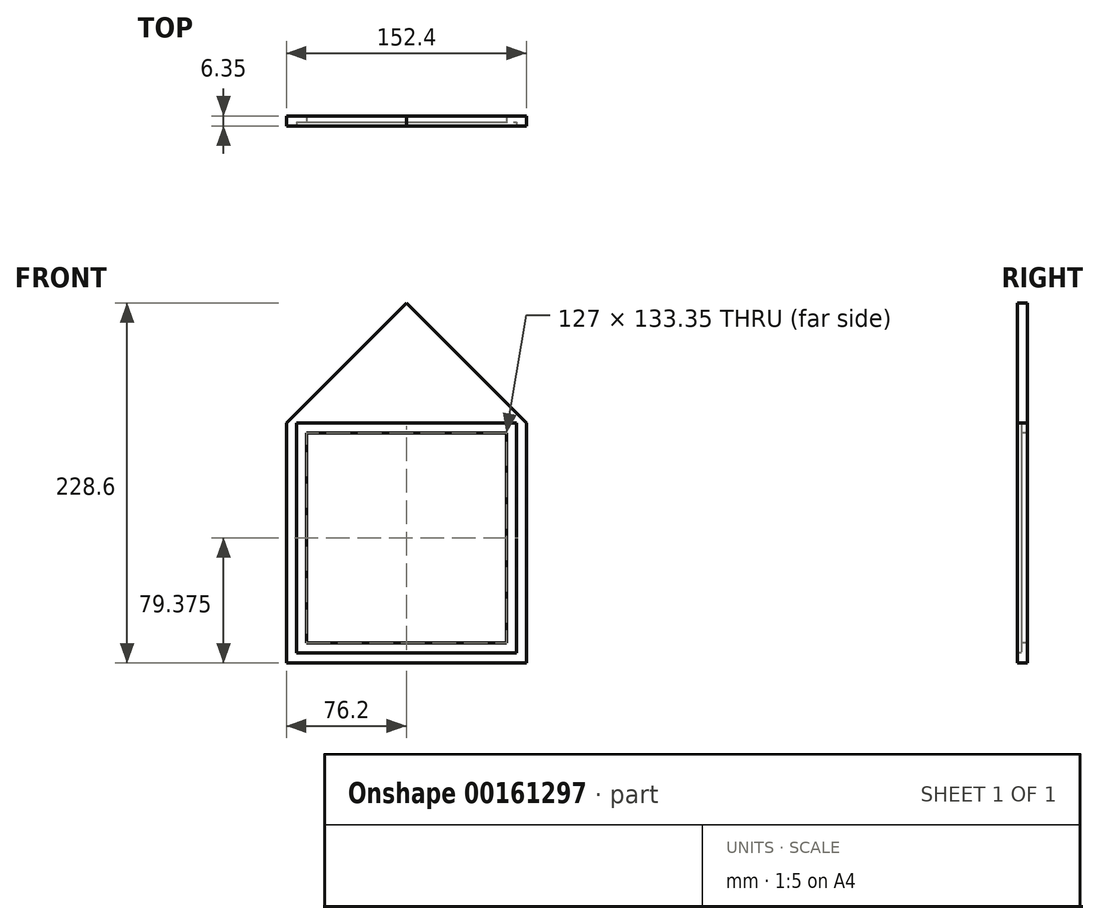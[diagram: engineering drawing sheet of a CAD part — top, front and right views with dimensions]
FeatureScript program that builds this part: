
annotation { "Feature Type Name" : "Feature", "Feature Type Description" : "" }
export const myFeature = defineFeature(function(context is Context, id is Id, definition is map)
    precondition{}
    {
        {
            var Q0;
            Q0=qCreatedBy(makeId("Front.planeOp"),FACE);
            var sketch = newSketch(context, id + "F0", { "sketchPlane" : qUnion([Q0])});
            skLineSegment(sketch, "E0.bottom", {"start": v(0, 0) * mm, "end": v(152.4, 0) * mm});
            skLineSegment(sketch, "E0.top", {"start": v(0, -152.4) * mm, "end": v(152.4, -152.4) * mm});
            skLineSegment(sketch, "E0.left", {"start": v(0, 0) * mm, "end": v(0, -152.4) * mm});
            skLineSegment(sketch, "E0.right", {"start": v(152.4, 0) * mm, "end": v(152.4, -152.4) * mm});
            skLineSegment(sketch, "E1", {"start": v(0, 0) * mm, "end": v(76.2, 76.2) * mm});
            skLineSegment(sketch, "E2", {"start": v(76.2, 76.2) * mm, "end": v(152.4, 0) * mm});
            skSolve(sketch);
        }
        {
            var Q0;
            Q0 = qSketchRegion(id + "F0", true);
            extrude(context, id + "F1", {"entities" : qUnion([Q0]), "depth" : 6.35 * mm});
        }
        {
            var Q0;
            Q0=makeQuery(id+"F1.opExtrude","CAP_FACE",FACE,{"disambiguationData":[OSD([sQuery(id+"F0.wireOp",EDGE,"E0.top"),sQuery(id+"F0.wireOp",EDGE,"E0.left"),sQuery(id+"F0.wireOp",EDGE,"E0.right"),sQuery(id+"F0.wireOp",EDGE,"E1"),sQuery(id+"F0.wireOp",EDGE,"E2")])],"isStart":false});
            var sketch = newSketch(context, id + "F2", { "sketchPlane" : qUnion([Q0])});
            skLineSegment(sketch, "E3.bottom", {"start": v(6.35, 0) * mm, "end": v(146.05, 0) * mm});
            skLineSegment(sketch, "E3.top", {"start": v(6.35, -146.05) * mm, "end": v(146.05, -146.05) * mm});
            skLineSegment(sketch, "E3.left", {"start": v(6.35, 0) * mm, "end": v(6.35, -146.05) * mm});
            skLineSegment(sketch, "E3.right", {"start": v(146.05, 0) * mm, "end": v(146.05, -146.05) * mm});
            skSolve(sketch);
        }
        {
            var Q0;
            Q0 = qSketchRegion(id + "F2", true);
            extrude(context, id + "F3", {"entities" : qUnion([Q0]), "operationType" : NewBodyOperationType.REMOVE, "oppositeDirection" : true, "depth" : 2.54 * mm});
        }
        {
            var Q0;
            Q0=makeQuery(id+"F3.boolean.opBoolean","COPY",FACE,{"derivedFrom":makeQuery(id+"F3.opExtrude","CAP_FACE",FACE,{"disambiguationData":[OSD([sQuery(id+"F2.wireOp",EDGE,"E3.bottom"),sQuery(id+"F2.wireOp",EDGE,"E3.top"),sQuery(id+"F2.wireOp",EDGE,"E3.left"),sQuery(id+"F2.wireOp",EDGE,"E3.right")])],"isStart":false})});
            var sketch = newSketch(context, id + "F4", { "sketchPlane" : qUnion([Q0])});
            skLineSegment(sketch, "E4.bottom", {"start": v(12.7, -6.35) * mm, "end": v(139.7, -6.35) * mm});
            skLineSegment(sketch, "E4.top", {"start": v(12.7, -139.7) * mm, "end": v(139.7, -139.7) * mm});
            skLineSegment(sketch, "E4.left", {"start": v(12.7, -6.35) * mm, "end": v(12.7, -139.7) * mm});
            skLineSegment(sketch, "E4.right", {"start": v(139.7, -6.35) * mm, "end": v(139.7, -139.7) * mm});
            skSolve(sketch);
        }
        {
            var Q0;
            Q0 = qSketchRegion(id + "F4", true);
            extrude(context, id + "F5", {"entities" : qUnion([Q0]), "operationType" : NewBodyOperationType.REMOVE, "endBound" : BoundingType.THROUGH_ALL, "oppositeDirection" : true, "depth" : 25.4 * mm});
        }
    });
